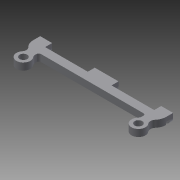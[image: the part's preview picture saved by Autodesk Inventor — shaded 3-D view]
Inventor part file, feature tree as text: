
AUTODESK INVENTOR PART (.ipt)
format: ipt  version: 2015 (Build 190159000, 159)  size: 261,120 bytes
history: native  units: in
note: dims shown in document units (in); Inventor stores cm internally (conversion verified against a paired STEP export)
features: extrude x7, pattern_linear x6, sketch x6, projected_geometry x3, fillet x2
ambient origin geometry x8: Origin, YZ Plane, XZ Plane, XY Plane, X Axis, Y Axis, Z Axis, Center Point
bodies: Solid1 (feature_tree)
feature tree (24):
  extrude  "Extrusion1"  Depth=1.95in
  extrude  "Extrusion2"  Depth=0.2362in
  extrude  "Extrusion3"  Depth=0.1181in TaperAngle=0.0deg
  pattern_linear  "Rectangular Pattern1"  Spacing1=0.1378in  [1 undecoded]
  extrude  "Extrusion4"  Depth=0.0787in
  pattern_linear  "Rectangular Pattern2"  Spacing1=0.0394in  [1 undecoded]
  pattern_linear  "Rectangular Pattern3"  Spacing1=0.0787in  [1 undecoded]
  extrude  "Extrusion5"  Depth=0.1181in TaperAngle=0.0deg
  extrude  "Extrusion6"  Depth=0.045in
  pattern_linear  "Rectangular Pattern4"  Spacing1=0.1181in  [1 undecoded]
  pattern_linear  "Rectangular Pattern5"  Spacing1=0.9544in  [1 undecoded]
  pattern_linear  "Rectangular Pattern6"  Spacing1=0.0787in  [1 undecoded]
  extrude  "Extrusion7"  Depth=0.0787in
  fillet  "Fillet2"  Radius=0.025in
  fillet  "Fillet3"  Radius=0.025in
  sketch  "Sketch1"  dims[d0=0.1299in d2=1.95in]
  sketch  "Sketch2"  dims[d3=0.1299in d4=0.2362in]
  sketch  "Sketch3"  dims[d11=0.2362in d12=0.1181in d13=0.0in]
  sketch  "Sketch4"  dims[d14=0.2417in]
  sketch  "Sketch7"  dims[d15=0.0866in]
  projected_geometry  "Projected Loop1"
  sketch  "Sketch9"  dims[d16=0.1378in d17=0.1378in d18=0.0866in d19=0.0394in d20=0.0787in d21=0.1181in d22=0.0in d23=0.045in d24=0.1181in d25=0.0in d26=0.9544in d27=0.0787in d28=0.0787in d29=0.025in d30=0.025in d31=0.0956in d32=0.7874in d34=0.925in d35=0.1181in d36=0.0in d37=0.7874in d39=0.2in d40=0.7874in d42=0.925in d43=0.1181in d44=0.0in d46=0.0472in d47=0.0in d48=0.7874in d50=0.925in d51=0.7874in d53=1.125in d54=0.7874in d56=2.05in d77=0.0394in d78=0.0in d86=0.0787in d87=0.0787in]
  projected_geometry  "Projected Loop5"
  projected_geometry  "Projected Loop6"
note: 6 required parameter values undecoded (feature->parameter linkage not recoverable at this tier; creation-order binding heuristic only, values carry confidence <= 0.55)
